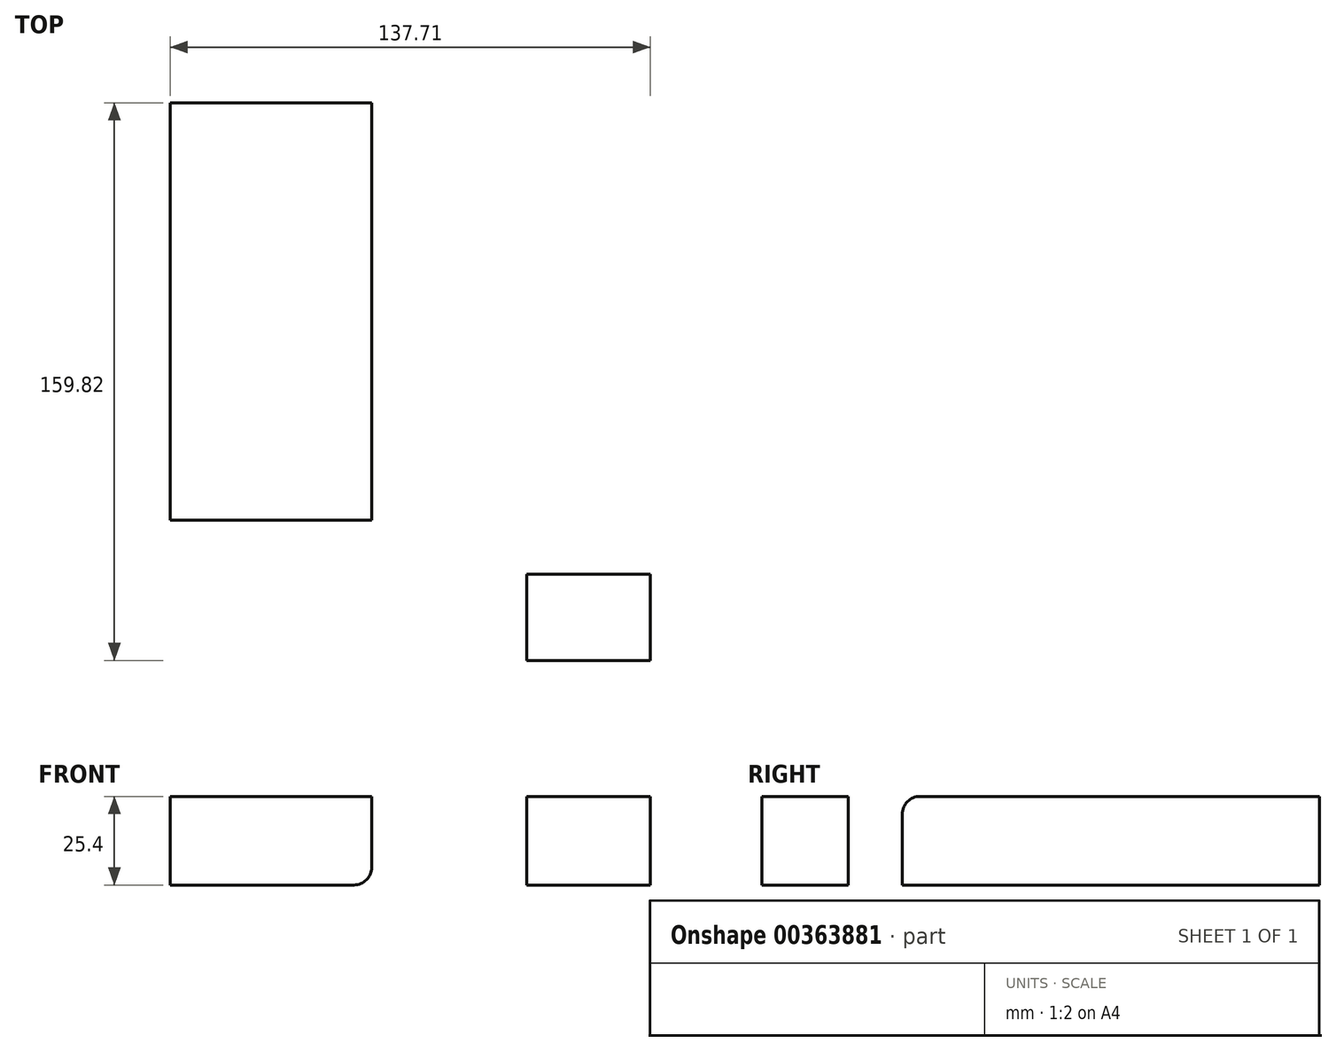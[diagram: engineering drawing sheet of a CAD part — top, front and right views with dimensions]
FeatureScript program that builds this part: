
annotation { "Feature Type Name" : "Feature", "Feature Type Description" : "" }
export const myFeature = defineFeature(function(context is Context, id is Id, definition is map)
    precondition{}
    {
        {
            var Q0;
            Q0=qCreatedBy(makeId("Top.planeOp"),FACE);
            var sketch = newSketch(context, id + "F0", { "sketchPlane" : qUnion([Q0])});
            skLineSegment(sketch, "E0.bottom", {"start": v(-35.44, 24.73) * mm, "end": v(0, 24.73) * mm});
            skLineSegment(sketch, "E0.top", {"start": v(-35.44, 0) * mm, "end": v(0, 0) * mm});
            skLineSegment(sketch, "E0.left", {"start": v(-35.44, 24.73) * mm, "end": v(-35.44, 0) * mm});
            skLineSegment(sketch, "E0.right", {"start": v(0, 24.73) * mm, "end": v(0, 0) * mm});
            skLineSegment(sketch, "E1.bottom", {"start": v(-79.94, 40.2) * mm, "end": v(-137.7, 40.2) * mm});
            skLineSegment(sketch, "E1.top", {"start": v(-79.94, 159.82) * mm, "end": v(-137.7, 159.82) * mm});
            skLineSegment(sketch, "E1.left", {"start": v(-79.94, 40.2) * mm, "end": v(-79.94, 159.82) * mm});
            skLineSegment(sketch, "E1.right", {"start": v(-137.7, 40.2) * mm, "end": v(-137.7, 159.82) * mm});
            skSolve(sketch);
        }
        {
            var Q0;
            Q0 = qSketchRegion(id + "F0", true);
            extrude(context, id + "F1", {"entities" : qUnion([Q0]), "depth" : 25.4 * mm});
        }
        {
            var Q0;
            Q0=makeQuery(id+"F1.opExtrude","CAP_EDGE",EDGE,{"disambiguationData":[OSD([sQuery(id+"F0.wireOp",EDGE,"E1.bottom")])],"isStart":false});
            var Q1;
            Q1=makeQuery(id+"F1.opExtrude","CAP_EDGE",EDGE,{"disambiguationData":[OSD([sQuery(id+"F0.wireOp",EDGE,"E1.left")])],"isStart":true});
            fillet(context, id + "F2", {"entities" : qUnion([Q0, Q1]), "radius" : 5.08 * mm, "tangentPropagation" : true, "allowEdgeOverflow" : false});
        }
    });
